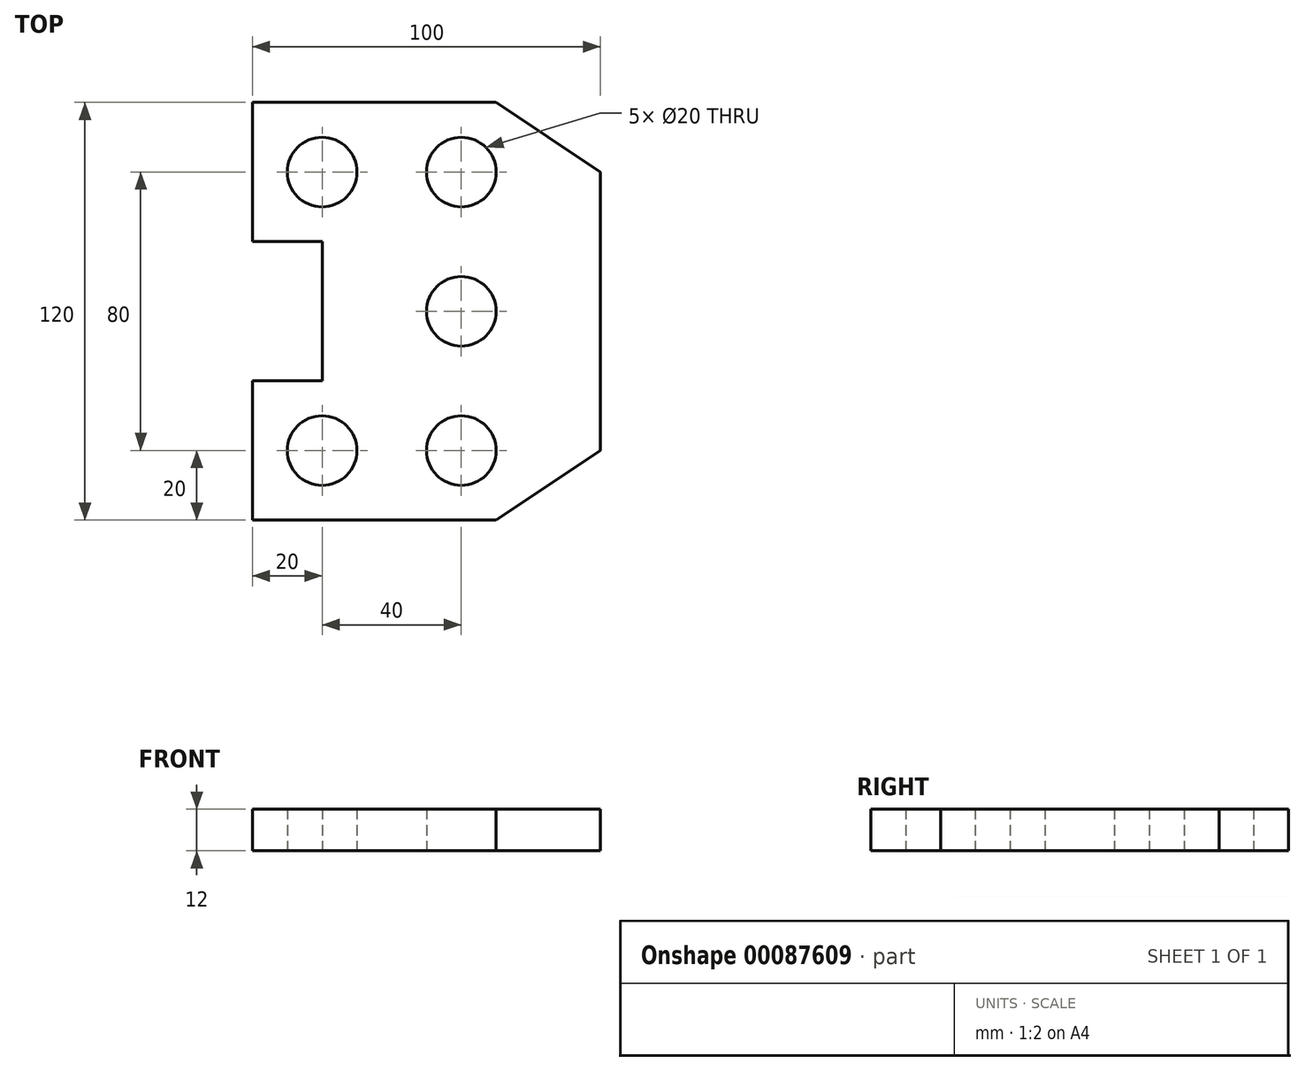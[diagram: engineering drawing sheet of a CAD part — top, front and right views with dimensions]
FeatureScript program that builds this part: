
annotation { "Feature Type Name" : "Feature", "Feature Type Description" : "" }
export const myFeature = defineFeature(function(context is Context, id is Id, definition is map)
    precondition{}
    {
        {
            var Q0;
            Q0=qCreatedBy(makeId("Top.planeOp"),FACE);
            var sketch = newSketch(context, id + "F0", { "sketchPlane" : qUnion([Q0])});
            skLineSegment(sketch, "E0.bottom", {"start": v(0, 0) * mm, "end": v(70, 0) * mm});
            skLineSegment(sketch, "E0.top", {"start": v(0, 120) * mm, "end": v(70, 120) * mm});
            skLineSegment(sketch, "E0.left", {"start": v(0, 0) * mm, "end": v(0, 40) * mm});
            skLineSegment(sketch, "E0.right", {"start": v(100, 20) * mm, "end": v(100, 100) * mm});
            skLineSegment(sketch, "E1.bottom", {"start": v(0, 40) * mm, "end": v(20, 40) * mm});
            skLineSegment(sketch, "E1.top", {"start": v(0, 80) * mm, "end": v(20, 80) * mm});
            skLineSegment(sketch, "E1.right", {"start": v(20, 40) * mm, "end": v(20, 80) * mm});
            skLineSegment(sketch, "E2", {"start": v(70, 0) * mm, "end": v(100, 20) * mm});
            skLineSegment(sketch, "E3", {"start": v(100, 100) * mm, "end": v(70, 120) * mm});
            skCircle(sketch, "E4", {"center": v(20, 100) * mm, "radius": 10 * mm});
            skLineSegment(sketch, "E5", {"start": v(20, 100) * mm, "end": v(60, 100) * mm, "construction": true});
            skLineSegment(sketch, "E6", {"start": v(60, 100) * mm, "end": v(60, 20) * mm, "construction": true});
            skLineSegment(sketch, "E7", {"start": v(60, 20) * mm, "end": v(20, 20) * mm, "construction": true});
            skCircle(sketch, "E8", {"center": v(60, 100) * mm, "radius": 10 * mm});
            skCircle(sketch, "E9", {"center": v(60, 60) * mm, "radius": 10 * mm});
            skCircle(sketch, "E10", {"center": v(60, 20) * mm, "radius": 10 * mm});
            skCircle(sketch, "E11", {"center": v(20, 20) * mm, "radius": 10 * mm});
            skLineSegment(sketch, "E12.trimOffspring", {"start": v(0, 80) * mm, "end": v(0, 120) * mm});
            skLineSegment(sketch, "E13", {"start": v(60, 20) * mm, "end": v(100, 20) * mm, "construction": true});
            skLineSegment(sketch, "E14", {"start": v(60, 100) * mm, "end": v(100, 100) * mm, "construction": true});
            skLineSegment(sketch, "E15", {"start": v(20, 80) * mm, "end": v(20, 100) * mm, "construction": true});
            skLineSegment(sketch, "E16", {"start": v(20, 40) * mm, "end": v(20, 20) * mm, "construction": true});
            skSolve(sketch);
        }
        {
            var Q0;
            Q0 = qSketchRegion(id + "F0", true);
            extrude(context, id + "F1", {"entities" : qUnion([Q0]), "depth" : 12 * mm});
        }
    });
